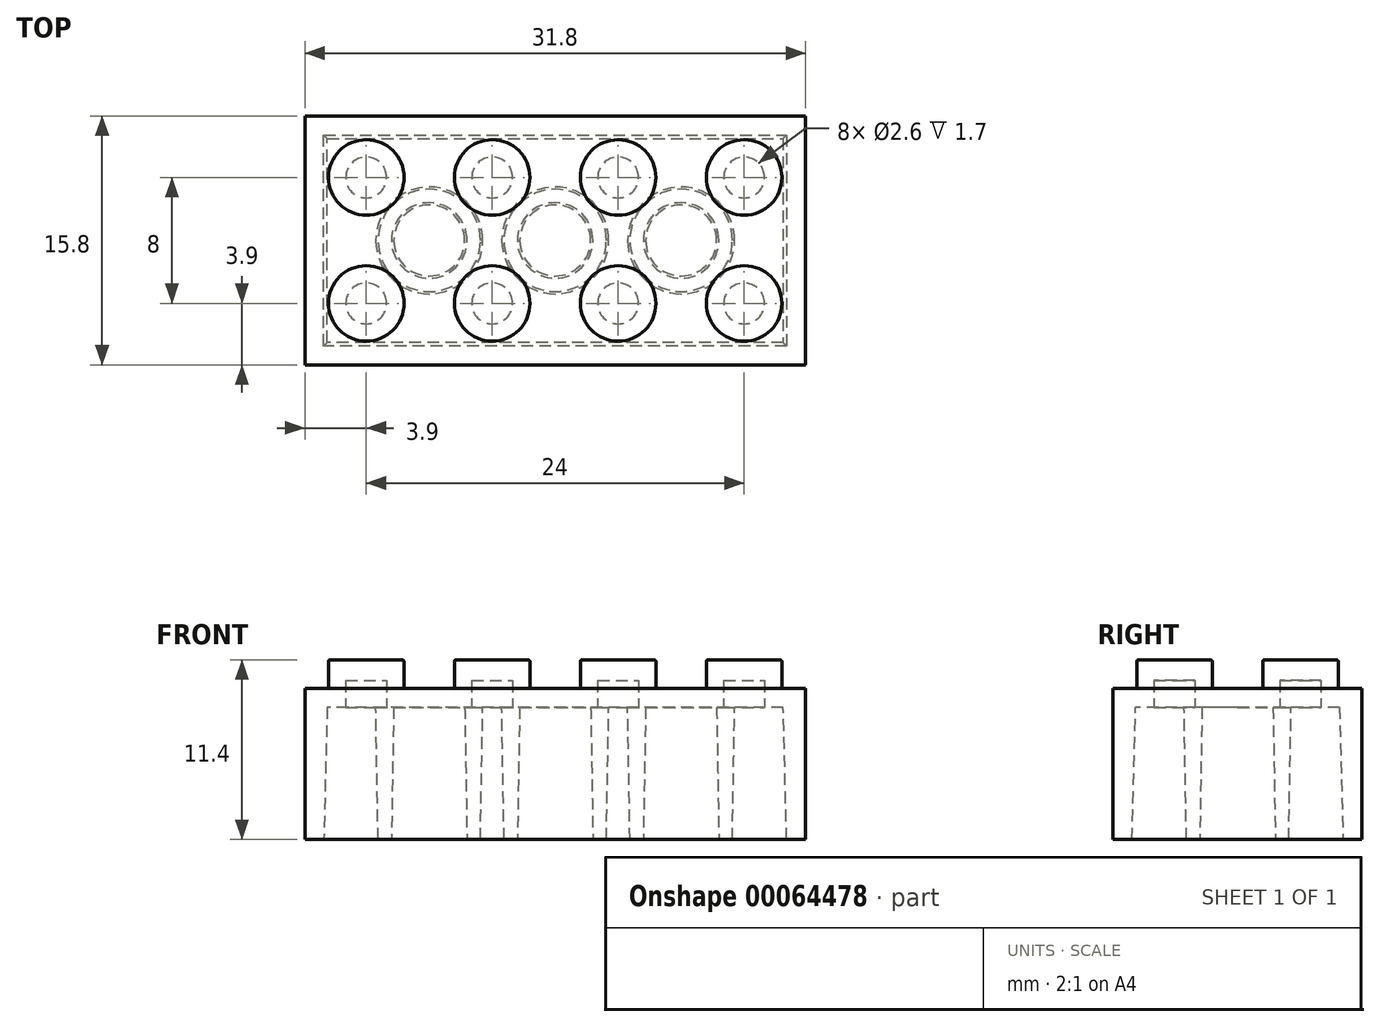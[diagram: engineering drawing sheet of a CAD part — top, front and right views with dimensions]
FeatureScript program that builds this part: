
annotation { "Feature Type Name" : "Feature", "Feature Type Description" : "" }
export const myFeature = defineFeature(function(context is Context, id is Id, definition is map)
    precondition{}
    {
        {
            var Q0;
            Q0=qCreatedBy(makeId("Top.planeOp"),FACE);
            var sketch = newSketch(context, id + "F0", { "sketchPlane" : qUnion([Q0])});
            skLineSegment(sketch, "E0.rect.bottom", {"start": v(15.9, -7.9) * mm, "end": v(-15.9, -7.9) * mm});
            skLineSegment(sketch, "E0.rect.top", {"start": v(15.9, 7.9) * mm, "end": v(-15.9, 7.9) * mm});
            skLineSegment(sketch, "E0.rect.left", {"start": v(15.9, -7.9) * mm, "end": v(15.9, 7.9) * mm});
            skLineSegment(sketch, "E0.rect.right", {"start": v(-15.9, -7.9) * mm, "end": v(-15.9, 7.9) * mm});
            skPoint(sketch, "E0.rect.middle", {"position": v(0, 0) * mm});
            skSolve(sketch);
        }
        {
            var Q0;
            Q0 = qSketchRegion(id + "F0", true);
            extrude(context, id + "F1", {"entities" : qUnion([Q0]), "depth" : 9.6 * mm});
        }
        {
            var Q0;
            Q0=qCreatedBy(makeId("Top.planeOp"),FACE);
            cPlane(context, id + "F2", {"entities" : qUnion([Q0]), "cplaneType" : CPlaneType.OFFSET, "offset" : 9.6 * mm, "width" : 150 * mm, "height" : 150 * mm});
        }
        {
            var Q0;
            Q0=qCreatedBy(id+"F2.planeOp",FACE);
            var sketch = newSketch(context, id + "F3", { "sketchPlane" : qUnion([Q0])});
            skCircle(sketch, "E1", {"center": v(-12, 4) * mm, "radius": 2.4 * mm});
            skCircle(sketch, "E2.1.0.0", {"center": v(-4, 4) * mm, "radius": 2.4 * mm});
            skCircle(sketch, "E2.2.0.0", {"center": v(4, 4) * mm, "radius": 2.4 * mm});
            skLineSegment(sketch, "E2.direction1", {"start": v(-12, 4) * mm, "end": v(-4, 4) * mm, "construction": true});
            skCircle(sketch, "E3.0.3.0", {"center": v(12, 4) * mm, "radius": 2.4 * mm});
            skCircle(sketch, "E4.0.1.0", {"center": v(-12, -4) * mm, "radius": 2.4 * mm});
            skCircle(sketch, "E4.1.1.0", {"center": v(-4, -4) * mm, "radius": 2.4 * mm});
            skCircle(sketch, "E4.2.1.0", {"center": v(4, -4) * mm, "radius": 2.4 * mm});
            skCircle(sketch, "E4.3.1.0", {"center": v(12, -4) * mm, "radius": 2.4 * mm});
            skLineSegment(sketch, "E4.direction2", {"start": v(-12, 4) * mm, "end": v(-12, -4) * mm, "construction": true});
            skSolve(sketch);
        }
        {
            var Q0;
            Q0 = qSketchRegion(id + "F3", true);
            extrude(context, id + "F4", {"entities" : qUnion([Q0]), "operationType" : NewBodyOperationType.ADD, "depth" : 1.8 * mm});
        }
        {
            var Q0;
            Q0=makeQuery(id+"F1.opExtrude","CAP_FACE",FACE,{"disambiguationData":[OSD([sQuery(id+"F0.wireOp",EDGE,"E0.rect.bottom"),sQuery(id+"F0.wireOp",EDGE,"E0.rect.top"),sQuery(id+"F0.wireOp",EDGE,"E0.rect.left"),sQuery(id+"F0.wireOp",EDGE,"E0.rect.right")])],"isStart":true});
            var sketch = newSketch(context, id + "F5", { "sketchPlane" : qUnion([Q0])});
            skLineSegment(sketch, "E5.0", {"start": v(14.7, 6.7) * mm, "end": v(-14.7, 6.7) * mm});
            skLineSegment(sketch, "E5.1", {"start": v(14.7, 6.7) * mm, "end": v(14.7, -6.7) * mm});
            skLineSegment(sketch, "E5.2", {"start": v(14.7, -6.7) * mm, "end": v(-14.7, -6.7) * mm});
            skLineSegment(sketch, "E5.3", {"start": v(-14.7, 6.7) * mm, "end": v(-14.7, -6.7) * mm});
            skSolve(sketch);
        }
        {
            var Q0;
            Q0 = qSketchRegion(id + "F5", true);
            extrude(context, id + "F6", {"entities" : qUnion([Q0]), "operationType" : NewBodyOperationType.REMOVE, "oppositeDirection" : true, "depth" : 8.4 * mm, "hasDraft" : true, "draftAngle" : 1.5 * degree, "draftPullDirection" : true});
        }
        {
            var Q0;
            Q0=makeQuery(id+"F6.boolean.opBoolean","COPY",FACE,{"derivedFrom":makeQuery(id+"F6.opExtrude","CAP_FACE",FACE,{"disambiguationData":[OSD([sQuery(id+"F5.wireOp",EDGE,"E5.0"),sQuery(id+"F5.wireOp",EDGE,"E5.1"),sQuery(id+"F5.wireOp",EDGE,"E5.2"),sQuery(id+"F5.wireOp",EDGE,"E5.3")])],"isStart":false})});
            var sketch = newSketch(context, id + "F7", { "sketchPlane" : qUnion([Q0])});
            skCircle(sketch, "E6.0", {"center": v(-12, 4) * mm, "radius": 2.4 * mm, "construction": true});
            skCircle(sketch, "E6.1", {"center": v(-12, -4) * mm, "radius": 2.4 * mm, "construction": true});
            skCircle(sketch, "E6.2", {"center": v(-4, 4) * mm, "radius": 2.4 * mm, "construction": true});
            skCircle(sketch, "E6.3", {"center": v(-4, -4) * mm, "radius": 2.4 * mm, "construction": true});
            skCircle(sketch, "E6.4", {"center": v(4, -4) * mm, "radius": 2.4 * mm, "construction": true});
            skCircle(sketch, "E6.5", {"center": v(4, 4) * mm, "radius": 2.4 * mm, "construction": true});
            skCircle(sketch, "E6.6", {"center": v(12, 4) * mm, "radius": 2.4 * mm, "construction": true});
            skCircle(sketch, "E6.7", {"center": v(12, -4) * mm, "radius": 2.4 * mm, "construction": true});
            skCircle(sketch, "E7", {"center": v(-12, 4) * mm, "radius": 1.3 * mm});
            skCircle(sketch, "E8", {"center": v(-4, 4) * mm, "radius": 1.3 * mm});
            skCircle(sketch, "E9", {"center": v(4, 4) * mm, "radius": 1.3 * mm});
            skCircle(sketch, "E10", {"center": v(12, 4) * mm, "radius": 1.3 * mm});
            skCircle(sketch, "E11", {"center": v(12, -4) * mm, "radius": 1.3 * mm});
            skCircle(sketch, "E12", {"center": v(4, -4) * mm, "radius": 1.3 * mm});
            skCircle(sketch, "E13", {"center": v(-4, -4) * mm, "radius": 1.3 * mm});
            skCircle(sketch, "E14", {"center": v(-12, -4) * mm, "radius": 1.3 * mm});
            skSolve(sketch);
        }
        {
            var Q0;
            Q0 = qSketchRegion(id + "F7", true);
            extrude(context, id + "F8", {"entities" : qUnion([Q0]), "operationType" : NewBodyOperationType.REMOVE, "oppositeDirection" : true, "depth" : 1.7 * mm});
        }
        {
            var Q0;
            Q0=qCreatedBy(makeId("Top.planeOp"),FACE);
            var sketch = newSketch(context, id + "F9", { "sketchPlane" : qUnion([Q0])});
            skLineSegment(sketch, "E15.0", {"start": v(-15.9, -7.9) * mm, "end": v(-15.9, 7.9) * mm, "construction": true});
            skLineSegment(sketch, "E16", {"start": v(-15.9, 0) * mm, "end": v(19.52, 0) * mm, "construction": true});
            skCircle(sketch, "E17", {"center": v(-8, 0) * mm, "radius": 3.25 * mm});
            skCircle(sketch, "E18", {"center": v(0, 0) * mm, "radius": 3.25 * mm});
            skCircle(sketch, "E19", {"center": v(8, 0) * mm, "radius": 3.25 * mm});
            skCircle(sketch, "E20.0", {"center": v(-12, -4) * mm, "radius": 1.3 * mm, "construction": true});
            skCircle(sketch, "E21.0", {"center": v(-4, 4) * mm, "radius": 1.3 * mm, "construction": true});
            skLineSegment(sketch, "E22", {"start": v(-12, -4) * mm, "end": v(-4, 4) * mm, "construction": true});
            skCircle(sketch, "E23", {"center": v(-8, 0) * mm, "radius": 2.4 * mm});
            skCircle(sketch, "E24", {"center": v(0, 0) * mm, "radius": 2.4 * mm});
            skCircle(sketch, "E25", {"center": v(8, 0) * mm, "radius": 2.4 * mm});
            skSolve(sketch);
        }
        {
            var Q0;
            Q0 = qSketchRegion(id + "F9", true);
            extrude(context, id + "F10", {"entities" : qUnion([Q0]), "operationType" : NewBodyOperationType.ADD, "endBound" : BoundingType.UP_TO_NEXT, "depth" : 8.4 * mm, "hasDraft" : true, "draftAngle" : 1 * degree});
        }
        {
            var Q0;
            Q0=makeQuery(id+"F4.opExtrude","CAP_EDGE",EDGE,{"disambiguationData":[OSD([sQuery(id+"F3.wireOp",EDGE,"E3.0.3.0")])],"isStart":false});
            var Q1;
            Q1=makeQuery(id+"F4.opExtrude","CAP_EDGE",EDGE,{"disambiguationData":[OSD([sQuery(id+"F3.wireOp",EDGE,"E4.3.1.0")])],"isStart":false});
            var Q2;
            Q2=makeQuery(id+"F4.opExtrude","CAP_EDGE",EDGE,{"disambiguationData":[OSD([sQuery(id+"F3.wireOp",EDGE,"E4.2.1.0")])],"isStart":false});
            var Q3;
            Q3=makeQuery(id+"F4.opExtrude","CAP_EDGE",EDGE,{"disambiguationData":[OSD([sQuery(id+"F3.wireOp",EDGE,"E2.2.0.0")])],"isStart":false});
            var Q4;
            Q4=makeQuery(id+"F4.opExtrude","CAP_EDGE",EDGE,{"disambiguationData":[OSD([sQuery(id+"F3.wireOp",EDGE,"E4.1.1.0")])],"isStart":false});
            var Q5;
            Q5=makeQuery(id+"F4.opExtrude","CAP_EDGE",EDGE,{"disambiguationData":[OSD([sQuery(id+"F3.wireOp",EDGE,"E2.1.0.0")])],"isStart":false});
            var Q6;
            Q6=makeQuery(id+"F4.opExtrude","CAP_EDGE",EDGE,{"disambiguationData":[OSD([sQuery(id+"F3.wireOp",EDGE,"E4.0.1.0")])],"isStart":false});
            var Q7;
            Q7=makeQuery(id+"F4.opExtrude","CAP_EDGE",EDGE,{"disambiguationData":[OSD([sQuery(id+"F3.wireOp",EDGE,"E1")])],"isStart":false});
            fillet(context, id + "F11", {"entities" : qUnion([Q0, Q1, Q2, Q3, Q4, Q5, Q6, Q7]), "radius" : 0.1 * mm, "tangentPropagation" : true, "allowEdgeOverflow" : false});
        }
    });
